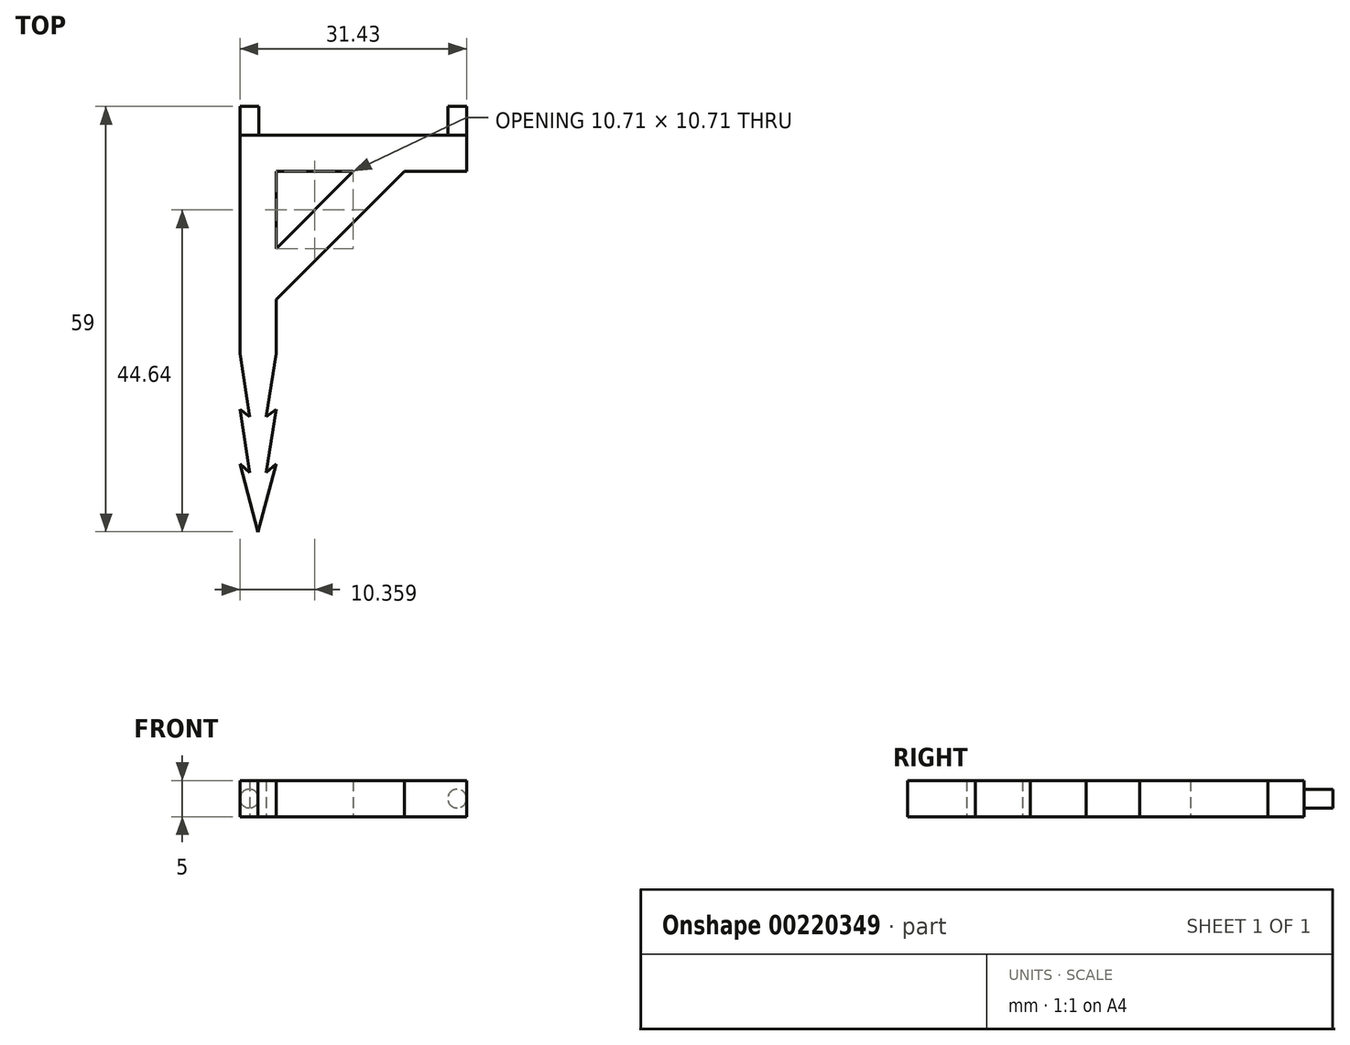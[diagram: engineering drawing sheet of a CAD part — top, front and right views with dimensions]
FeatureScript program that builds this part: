
annotation { "Feature Type Name" : "Feature", "Feature Type Description" : "" }
export const myFeature = defineFeature(function(context is Context, id is Id, definition is map)
    precondition{}
    {
        {
            assignVariable(context, id + "F0", {"name" : "Thickness", "anyValue" : 5});
        }
        {
            var Q0;
            Q0=qCreatedBy(makeId("Top.planeOp"),FACE);
            var sketch = newSketch(context, id + "F1", { "sketchPlane" : qUnion([Q0])});
            skLineSegment(sketch, "E0.bottom", {"start": v(-20.43, 89.36) * mm, "end": v(-15.43, 89.36) * mm});
            skLineSegment(sketch, "E0.top", {"start": v(-20.43, 39.36) * mm, "end": v(-15.43, 39.36) * mm});
            skLineSegment(sketch, "E0.left", {"start": v(-20.43, 89.36) * mm, "end": v(-20.43, 39.36) * mm});
            skLineSegment(sketch, "E0.right", {"start": v(-15.43, 89.36) * mm, "end": v(-15.43, 39.36) * mm});
            skLineSegment(sketch, "E1.bottom", {"start": v(-20.43, 89.36) * mm, "end": v(11, 89.36) * mm});
            skLineSegment(sketch, "E1.top", {"start": v(-20.43, 94.36) * mm, "end": v(11, 94.36) * mm});
            skLineSegment(sketch, "E1.left", {"start": v(-20.43, 89.36) * mm, "end": v(-20.43, 94.36) * mm});
            skLineSegment(sketch, "E1.right", {"start": v(11, 89.36) * mm, "end": v(11, 94.36) * mm});
            skLineSegment(sketch, "E2", {"start": v(-4.72, 89.36) * mm, "end": v(-15.43, 78.64) * mm});
            skLineSegment(sketch, "E3", {"start": v(2.36, 89.36) * mm, "end": v(-15.43, 71.57) * mm});
            skSolve(sketch);
        }
        {
            var Q0;
            Q0=makeQuery(id+"F1.imprint","IMPRINT",FACE,{"disambiguationData":[TD([[makeQuery(id+"F1.imprint","IMPRINT",EDGE,{"derivedFrom":sQuery(id+"F1.wireOp",EDGE,"E1.top")}),-1.0]])]});
            var Q1;
            Q1=makeQuery(id+"F1.imprint","IMPRINT",FACE,{"disambiguationData":[TD([[makeQuery(id+"F1.imprint","IMPRINT",EDGE,{"derivedFrom":sQuery(id+"F1.wireOp",EDGE,"E0.top")}),1.0]])]});
            var Q2;
            {var subQ0=sQuery(id+"F1.wireOp",EDGE,"E2");Q2=makeQuery(id+"F1.imprint","IMPRINT",FACE,{"disambiguationData":[TD([[makeQuery(id+"F1.imprint","IMPRINT",EDGE,{"derivedFrom":subQ0}),1.0]])]});}
            extrude(context, id + "F2", {"entities" : qUnion([Q0, Q1, Q2]), "depth" : (getVariable(context, 'Thickness')) * mm});
        }
        {
            var Q0;
            Q0=makeQuery(id+"F2.opExtrude","SWEPT_FACE",FACE,{"disambiguationData":[OSD([sQuery(id+"F1.wireOp",EDGE,"E1.top")])]});
            var sketch = newSketch(context, id + "F3", { "sketchPlane" : qUnion([Q0])});
            skLineSegment(sketch, "E4", {"start": v(-11, 2.5) * mm, "end": v(20.43, 2.5) * mm});
            skCircle(sketch, "E5", {"center": v(-9.7, 2.5) * mm, "radius": 1.3 * mm});
            skCircle(sketch, "E6", {"center": v(19.13, 2.5) * mm, "radius": 1.3 * mm});
            skSolve(sketch);
        }
        {
            var Q0;
            Q0=makeQuery(id+"F3.imprint","IMPRINT",FACE,{"disambiguationData":[TD([[makeQuery(id+"F3.imprint","IMPRINT",EDGE,{"derivedFrom":sQuery(id+"F3.wireOp",EDGE,"E5")}),1.0]])]});
            var Q1;
            {var subQ0=sQuery(id+"F3.wireOp",EDGE,"E6");var subQ1=sQuery(id+"F3.wireOp",EDGE,"E4");var subQ3=makeQuery(id+"F3.imprint","INTERSECT",VERTEX,{"derivedFrom":[subQ1,subQ0]});Q1=makeQuery(id+"F3.imprint","IMPRINT",FACE,{"disambiguationData":[TD([[makeQuery(id+"F3.imprint","IMPRINT",EDGE,{"disambiguationData":[TD([[subQ3,-1.0]])],"derivedFrom":subQ1}),-1.0]])]});}
            var Q2;
            {var subQ0=sQuery(id+"F3.wireOp",EDGE,"E6");var subQ1=sQuery(id+"F3.wireOp",EDGE,"E4");var subQ3=makeQuery(id+"F3.imprint","INTERSECT",VERTEX,{"derivedFrom":[subQ1,subQ0]});Q2=makeQuery(id+"F3.imprint","IMPRINT",FACE,{"disambiguationData":[TD([[makeQuery(id+"F3.imprint","IMPRINT",EDGE,{"disambiguationData":[TD([[subQ3,-1.0]])],"derivedFrom":subQ1}),1.0]])]});}
            extrude(context, id + "F4", {"entities" : qUnion([Q0, Q1, Q2]), "operationType" : NewBodyOperationType.ADD, "depth" : (getVariable(context, 'Thickness') - 1) * mm});
        }
        {
            var Q0;
            Q0=makeQuery(id+"F2.opExtrude","CAP_FACE",FACE,{"disambiguationData":[OSD([sQuery(id+"F1.wireOp",EDGE,"E0.top"),sQuery(id+"F1.wireOp",EDGE,"E0.left"),sQuery(id+"F1.wireOp",EDGE,"E0.right"),sQuery(id+"F1.wireOp",EDGE,"E1.bottom"),sQuery(id+"F1.wireOp",EDGE,"E1.top"),sQuery(id+"F1.wireOp",EDGE,"E1.left"),sQuery(id+"F1.wireOp",EDGE,"E1.right"),sQuery(id+"F1.wireOp",EDGE,"E2"),sQuery(id+"F1.wireOp",EDGE,"E3")])],"isStart":true});
            var sketch = newSketch(context, id + "F5", { "sketchPlane" : qUnion([Q0])});
            skLineSegment(sketch, "E7", {"start": v(-17.93, -39.36) * mm, "end": v(-15.43, -48.76) * mm});
            skLineSegment(sketch, "E8", {"start": v(-15.43, -48.76) * mm, "end": v(-16.81, -47.55) * mm});
            skLineSegment(sketch, "E9", {"start": v(-16.81, -47.55) * mm, "end": v(-15.43, -56.36) * mm});
            skLineSegment(sketch, "E10", {"start": v(-15.43, -56.36) * mm, "end": v(-16.81, -55.3) * mm});
            skLineSegment(sketch, "E11", {"start": v(-16.81, -55.3) * mm, "end": v(-15.43, -64.1) * mm});
            skLineSegment(sketch, "E12", {"start": v(-15.43, -64.1) * mm, "end": v(-20.43, -64.1) * mm});
            skLineSegment(sketch, "E13", {"start": v(-20.43, -64.1) * mm, "end": v(-19.1, -55.3) * mm});
            skLineSegment(sketch, "E14", {"start": v(-19.1, -55.3) * mm, "end": v(-20.43, -56.36) * mm});
            skLineSegment(sketch, "E15", {"start": v(-20.43, -56.36) * mm, "end": v(-19.1, -47.55) * mm});
            skLineSegment(sketch, "E16", {"start": v(-19.1, -47.55) * mm, "end": v(-20.43, -48.76) * mm});
            skLineSegment(sketch, "E17", {"start": v(-20.43, -48.76) * mm, "end": v(-17.93, -39.36) * mm});
            skLineSegment(sketch, "E18", {"start": v(-17.93, -39.36) * mm, "end": v(-17.93, -64.1) * mm});
            skSolve(sketch);
        }
        {
            var Q0;
            {var subQ0=sQuery(id+"F5.wireOp",EDGE,"E7");Q0=makeQuery(id+"F5.imprint","IMPRINT",FACE,{"disambiguationData":[TD([[makeQuery(id+"F5.imprint","IMPRINT",EDGE,{"derivedFrom":subQ0}),1.0]])]});}
            var Q1;
            {var subQ0=sQuery(id+"F5.wireOp",EDGE,"E17");Q1=makeQuery(id+"F5.imprint","IMPRINT",FACE,{"disambiguationData":[TD([[makeQuery(id+"F5.imprint","IMPRINT",EDGE,{"derivedFrom":subQ0}),1.0]])]});}
            var Q2;
            {var subQ0=sQuery(id+"F5.wireOp",EDGE,"E15");Q2=makeQuery(id+"F5.imprint","IMPRINT",FACE,{"disambiguationData":[TD([[makeQuery(id+"F5.imprint","IMPRINT",EDGE,{"derivedFrom":subQ0}),1.0]])]});}
            var Q3;
            {var subQ0=sQuery(id+"F5.wireOp",EDGE,"E8");Q3=makeQuery(id+"F5.imprint","IMPRINT",FACE,{"disambiguationData":[TD([[makeQuery(id+"F5.imprint","IMPRINT",EDGE,{"derivedFrom":subQ0}),1.0]])]});}
            var Q4;
            {var subQ0=sQuery(id+"F5.wireOp",EDGE,"E10");Q4=makeQuery(id+"F5.imprint","IMPRINT",FACE,{"disambiguationData":[TD([[makeQuery(id+"F5.imprint","IMPRINT",EDGE,{"derivedFrom":subQ0}),1.0]])]});}
            var Q5;
            {var subQ0=sQuery(id+"F5.wireOp",EDGE,"E13");Q5=makeQuery(id+"F5.imprint","IMPRINT",FACE,{"disambiguationData":[TD([[makeQuery(id+"F5.imprint","IMPRINT",EDGE,{"derivedFrom":subQ0}),1.0]])]});}
            extrude(context, id + "F6", {"entities" : qUnion([Q0, Q1, Q2, Q3, Q4, Q5]), "operationType" : NewBodyOperationType.REMOVE, "endBound" : BoundingType.UP_TO_NEXT, "oppositeDirection" : true, "depth" : 25 * mm});
        }
    });
